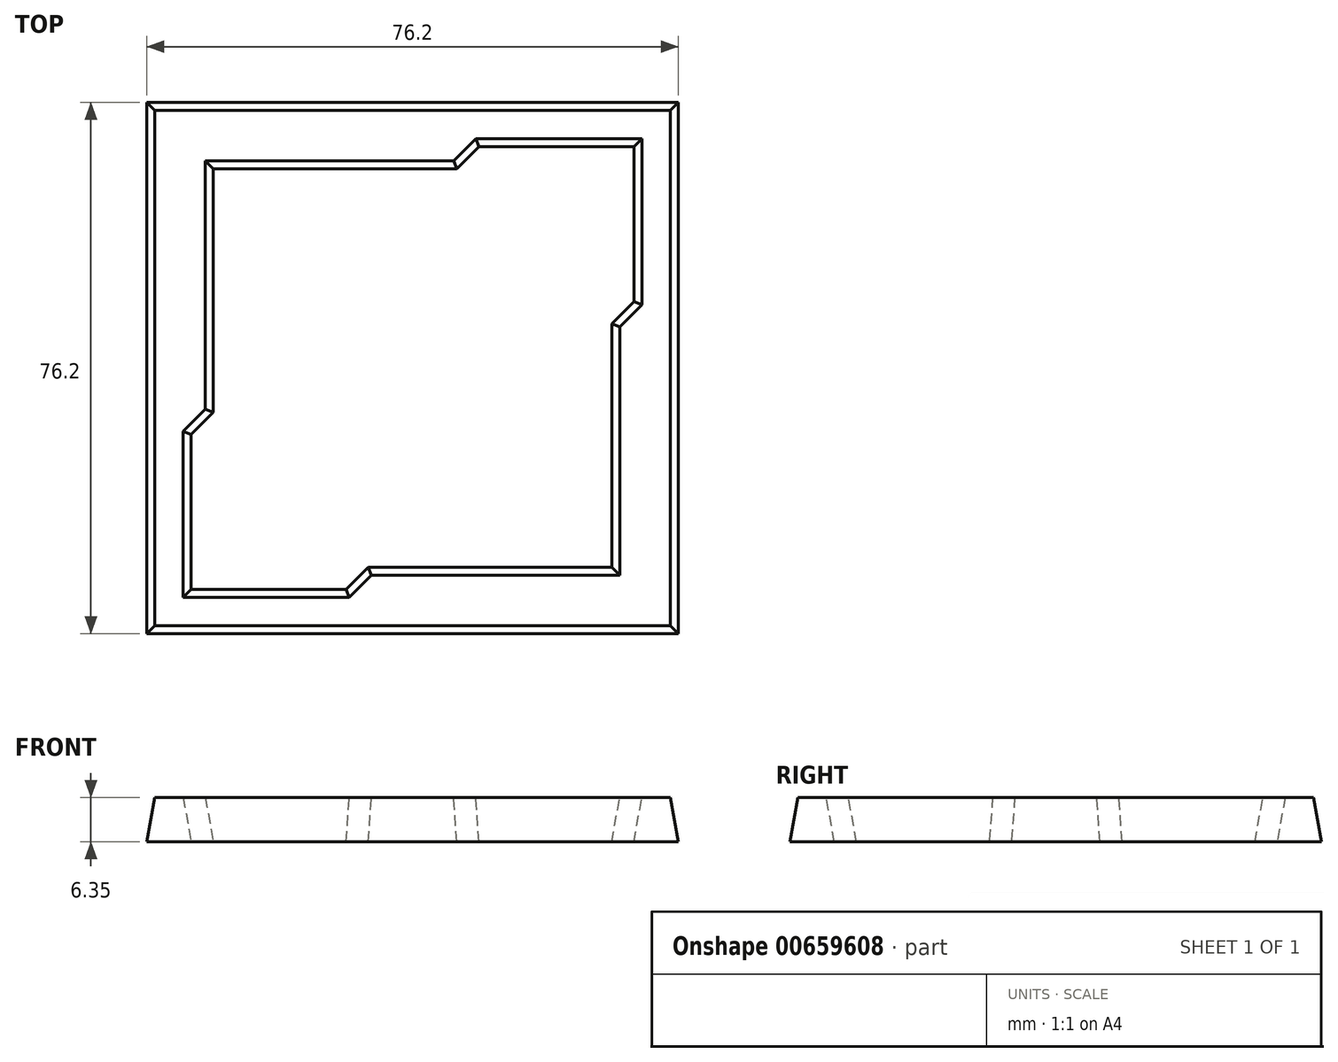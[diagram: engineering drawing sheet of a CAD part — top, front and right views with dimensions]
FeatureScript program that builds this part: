
annotation { "Feature Type Name" : "Feature", "Feature Type Description" : "" }
export const myFeature = defineFeature(function(context is Context, id is Id, definition is map)
    precondition{}
    {
        {
            var Q0;
            Q0=qCreatedBy(makeId("Top.planeOp"),FACE);
            var sketch = newSketch(context, id + "F0", { "sketchPlane" : qUnion([Q0])});
            skLineSegment(sketch, "E0.bottom", {"start": v(25.4, -25.4) * mm, "end": v(-25.4, -25.4) * mm});
            skLineSegment(sketch, "E0.top", {"start": v(25.4, 25.4) * mm, "end": v(-25.4, 25.4) * mm});
            skLineSegment(sketch, "E0.left", {"start": v(25.4, -25.4) * mm, "end": v(25.4, 25.4) * mm});
            skLineSegment(sketch, "E0.right", {"start": v(-25.4, -25.4) * mm, "end": v(-25.4, 25.4) * mm});
            skPoint(sketch, "E0.middle", {"position": v(0, 0) * mm});
            skLineSegment(sketch, "E1.bottom", {"start": v(31.75, -31.75) * mm, "end": v(-31.75, -31.75) * mm});
            skLineSegment(sketch, "E1.top", {"start": v(31.75, 31.75) * mm, "end": v(-31.75, 31.75) * mm});
            skLineSegment(sketch, "E1.left", {"start": v(31.75, -31.75) * mm, "end": v(31.75, 31.75) * mm});
            skLineSegment(sketch, "E1.right", {"start": v(-31.75, -31.75) * mm, "end": v(-31.75, 31.75) * mm});
            skLineSegment(sketch, "E2.bottom", {"start": v(38.1, -38.1) * mm, "end": v(-38.1, -38.1) * mm});
            skLineSegment(sketch, "E2.top", {"start": v(38.1, 38.1) * mm, "end": v(-38.1, 38.1) * mm});
            skLineSegment(sketch, "E2.left", {"start": v(38.1, -38.1) * mm, "end": v(38.1, 38.1) * mm});
            skLineSegment(sketch, "E2.right", {"start": v(-38.1, -38.1) * mm, "end": v(-38.1, 38.1) * mm});
            skLineSegment(sketch, "E3.bottom", {"start": v(28.57, -28.57) * mm, "end": v(-28.58, -28.58) * mm});
            skLineSegment(sketch, "E3.top", {"start": v(28.58, 28.58) * mm, "end": v(-28.57, 28.57) * mm});
            skLineSegment(sketch, "E3.left", {"start": v(28.57, -28.57) * mm, "end": v(28.58, 28.58) * mm});
            skLineSegment(sketch, "E3.right", {"start": v(-28.58, -28.58) * mm, "end": v(-28.57, 28.57) * mm});
            skLineSegment(sketch, "E4", {"start": v(-28.57, 28.57) * mm, "end": v(-25.4, 25.4) * mm});
            skLineSegment(sketch, "E5", {"start": v(28.57, -28.57) * mm, "end": v(25.4, -25.4) * mm});
            skPoint(sketch, "E6", {"position": v(6.35, 28.58) * mm});
            skLineSegment(sketch, "E7", {"start": v(6.35, 28.58) * mm, "end": v(9.52, 31.75) * mm});
            skPoint(sketch, "E8", {"position": v(-31.75, 31.75) * mm});
            skLineSegment(sketch, "E9", {"start": v(31.75, 9.53) * mm, "end": v(28.58, 6.35) * mm});
            skLineSegment(sketch, "E10", {"start": v(-9.52, -31.75) * mm, "end": v(-6.35, -28.58) * mm});
            skLineSegment(sketch, "E11", {"start": v(-31.75, -9.52) * mm, "end": v(-28.58, -6.35) * mm});
            skSolve(sketch);
        }
        {
            var Q0;
            Q0=makeQuery(id+"F0.imprint","IMPRINT",FACE,{"disambiguationData":[TD([[makeQuery(id+"F0.imprint","IMPRINT",EDGE,{"derivedFrom":sQuery(id+"F0.wireOp",EDGE,"E2.bottom")}),-1.0]])]});
            var Q1;
            {var subQ4=sQuery(id+"F0.wireOp",EDGE,"E7");Q1=makeQuery(id+"F0.imprint","IMPRINT",FACE,{"disambiguationData":[TD([[makeQuery(id+"F0.imprint","IMPRINT",EDGE,{"derivedFrom":subQ4}),1.0]])]});}
            var Q2;
            {var subQ3=sQuery(id+"F0.wireOp",EDGE,"E9");Q2=makeQuery(id+"F0.imprint","IMPRINT",FACE,{"disambiguationData":[TD([[makeQuery(id+"F0.imprint","IMPRINT",EDGE,{"derivedFrom":subQ3}),1.0]])]});}
            extrude(context, id + "F1", {"entities" : qUnion([Q0, Q1, Q2]), "depth" : 6.35 * mm, "offsetDistance" : 25.4 * mm, "hasDraft" : true, "draftAngle" : 10 * degree, "draftPullDirection" : true});
        }
    });
